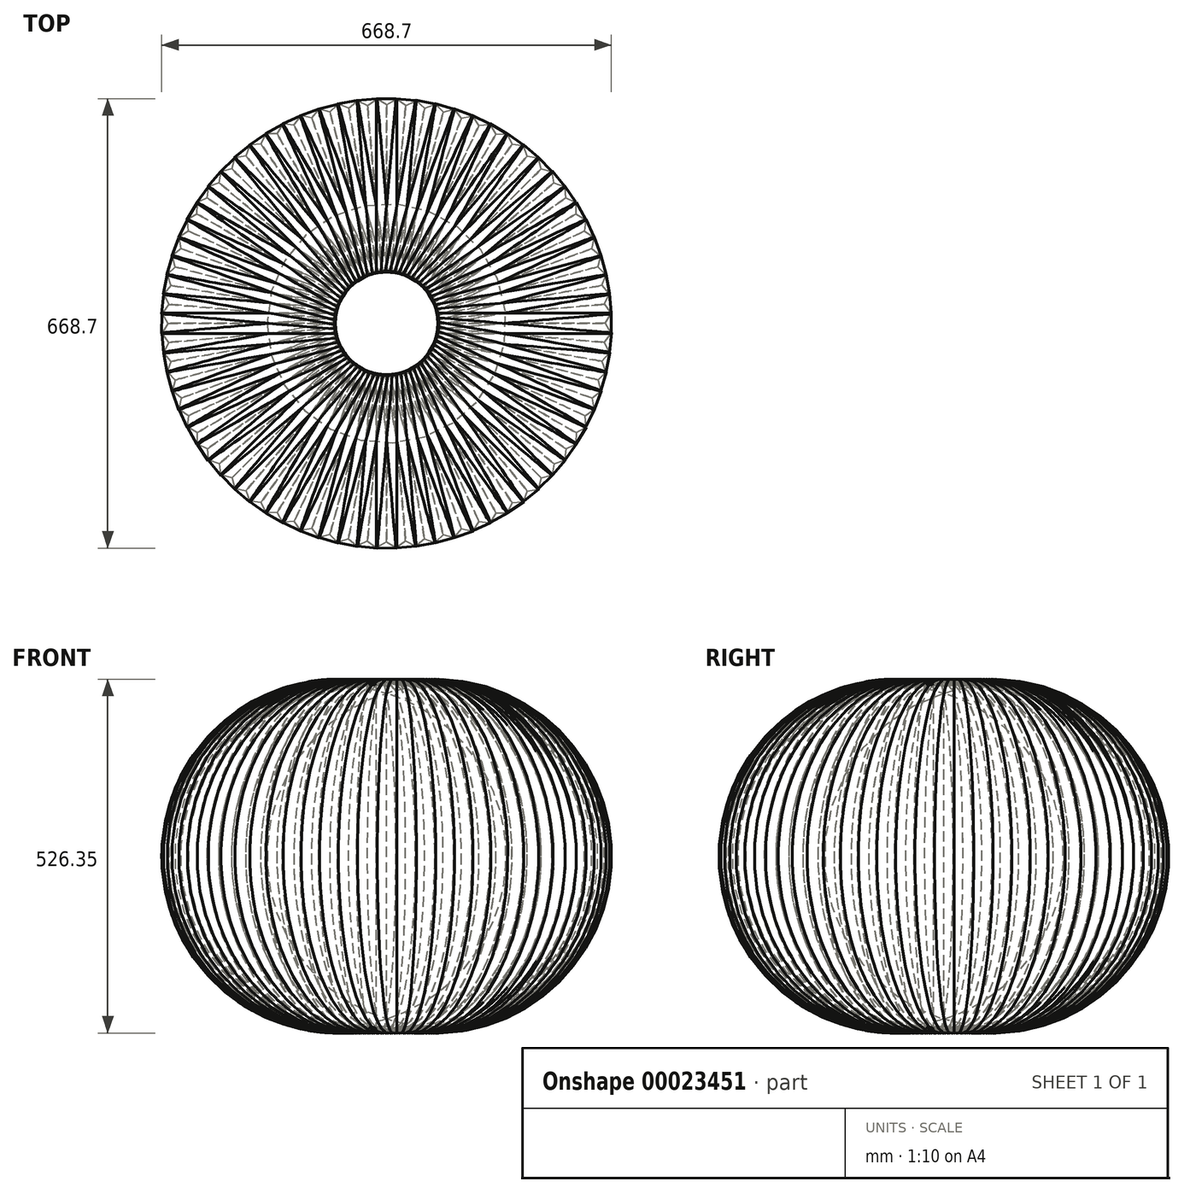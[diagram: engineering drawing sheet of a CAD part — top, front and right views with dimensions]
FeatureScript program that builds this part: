
annotation { "Feature Type Name" : "Feature", "Feature Type Description" : "" }
export const myFeature = defineFeature(function(context is Context, id is Id, definition is map)
    precondition{}
    {
        {
            var Q0;
            Q0=qCreatedBy(makeId("Front.planeOp"),FACE);
            var sketch = newSketch(context, id + "F0", { "sketchPlane" : qUnion([Q0])});
            skLineSegment(sketch, "E0", {"start": v(0, 492.91) * mm, "end": v(0, -560.81) * mm, "construction": true});
            skLineSegment(sketch, "E1.bottom", {"start": v(0, 254) * mm, "end": v(-76.2, 254) * mm});
            skLineSegment(sketch, "E1.top", {"start": v(0, -254) * mm, "end": v(-76.2, -254) * mm});
            skLineSegment(sketch, "E1.left", {"start": v(0, 254) * mm, "end": v(0, -254) * mm});
            skLineSegment(sketch, "E1.right", {"start": v(-76.2, 254) * mm, "end": v(-76.2, -254) * mm});
            skArc(sketch, "E2", {"start": v(-76.2, 254) * mm, "mid": v(-330.2, 0) * mm, "end": v(-76.2, -254) * mm});
            skSolve(sketch);
        }
        {
            var Q0;
            Q0=makeQuery(id+"F0.imprint","IMPRINT",FACE,{"disambiguationData":[TD([[makeQuery(id+"F0.imprint","IMPRINT",EDGE,{"derivedFrom":sQuery(id+"F0.wireOp",EDGE,"E1.right")}),-1.0]])]});
            var Q1;
            Q1=makeQuery(id+"F0.imprint","IMPRINT",FACE,{"disambiguationData":[TD([[makeQuery(id+"F0.imprint","IMPRINT",EDGE,{"derivedFrom":sQuery(id+"F0.wireOp",EDGE,"E1.bottom")}),1.0]])]});
            var Q2;
            Q2=sQuery(id+"F0.wireOp",EDGE,"E0");
            revolve(context, id + "F1", {"entities" : qUnion([Q0, Q1]), "axis" : qUnion([Q2]), "revolveType" : RevolveType.FULL});
        }
        {
            var Q0;
            Q0=qCreatedBy(makeId("Front.planeOp"),FACE);
            var sketch = newSketch(context, id + "F2", { "sketchPlane" : qUnion([Q0])});
            skLineSegment(sketch, "E3", {"start": v(0, 760) * mm, "end": v(0, -293.71) * mm, "construction": true});
            skLineSegment(sketch, "E4.bottom", {"start": v(0, 254) * mm, "end": v(-76.2, 254) * mm});
            skLineSegment(sketch, "E4.top", {"start": v(0, -254) * mm, "end": v(-76.2, -254) * mm});
            skLineSegment(sketch, "E4.left", {"start": v(0, 254) * mm, "end": v(0, -254) * mm});
            skLineSegment(sketch, "E4.right", {"start": v(-76.2, 254) * mm, "end": v(-76.2, -254) * mm});
            skArc(sketch, "E5", {"start": v(-76.2, 254) * mm, "mid": v(-330.2, 0) * mm, "end": v(-76.2, -254) * mm});
            skArc(sketch, "E6", {"start": v(-76.2, 254) * mm, "mid": v(-325.12, 0) * mm, "end": v(-76.2, -254) * mm});
            skLineSegment(sketch, "E7", {"start": v(-71.07, 0) * mm, "end": v(-76.2, -254) * mm, "construction": true});
            skSolve(sketch);
        }
        {
            var Q0;
            Q0=sQuery(id+"F2.wireOp",EDGE,"E4.right");
            cPlane(context, id + "F3", {"entities" : qUnion([Q0]), "cplaneType" : CPlaneType.LINE_ANGLE, "offset" : 152.4 * mm, "angle" : 180 * degree, "width" : 152.4 * mm, "height" : 152.4 * mm});
        }
        {
            var Q0;
            Q0=qCreatedBy(id+"F3.planeOp",FACE);
            var sketch = newSketch(context, id + "F4", { "sketchPlane" : qUnion([Q0])});
            skLineSegment(sketch, "E8", {"start": v(16.43, -254) * mm, "end": v(0, -254) * mm});
            skLineSegment(sketch, "E9", {"start": v(0, -254) * mm, "end": v(0, -244.51) * mm});
            skLineSegment(sketch, "E10", {"start": v(0, -244.51) * mm, "end": v(0, -254) * mm});
            skLineSegment(sketch, "E11", {"start": v(0, -254) * mm, "end": v(0, -261.75) * mm, "construction": true});
            skLineSegment(sketch, "E12", {"start": v(16.43, -254) * mm, "end": v(-17.03, -254.34) * mm});
            skLineSegment(sketch, "E13", {"start": v(15.24, -262.76) * mm, "end": v(0, -254.17) * mm});
            skLineSegment(sketch, "E14", {"start": v(0, -254.17) * mm, "end": v(0, -254) * mm});
            skLineSegment(sketch, "E15", {"start": v(-15.24, -263.18) * mm, "end": v(0, -254.17) * mm});
            skLineSegment(sketch, "E16", {"start": v(-15.24, -263.18) * mm, "end": v(15.24, -262.76) * mm});
            skSolve(sketch);
        }
        {
            var Q0;
            Q0=makeQuery(id+"F4.imprint","IMPRINT",FACE,{"disambiguationData":[TD([[makeQuery(id+"F4.imprint","IMPRINT",EDGE,{"derivedFrom":sQuery(id+"F4.wireOp",EDGE,"E13")}),1.0]])]});
            var Q1;
            Q1=sQuery(id+"F2.wireOp",EDGE,"E6");
            sweep(context, id + "F5", {"profiles" : qUnion([Q0]), "path" : qUnion([Q1])});
        }
        {
            var Q0;
            Q0=makeQuery(id+"F5.opSweep","SWEPT_BODY",BODY,{"disambiguationData":[OSD([sQuery(id+"F2.wireOp",EDGE,"E6"),sQuery(id+"F4.wireOp",EDGE,"E13"),sQuery(id+"F4.wireOp",EDGE,"E15"),sQuery(id+"F4.wireOp",EDGE,"E16")])]});
            var Q1;
            Q1=makeQuery(id+"F5.boolean.opBoolean","COPY",FACE,{"derivedFrom":makeQuery(id+"F5.opSweep","SWEPT_FACE",FACE,{"disambiguationData":[OSD([sQuery(id+"F2.wireOp",EDGE,"E6"),sQuery(id+"F4.wireOp",EDGE,"E15")])]})});
            var Q2;
            Q2=makeQuery(id+"F5.boolean.opBoolean","COPY",FACE,{"derivedFrom":makeQuery(id+"F5.opSweep","SWEPT_FACE",FACE,{"disambiguationData":[OSD([sQuery(id+"F2.wireOp",EDGE,"E6"),sQuery(id+"F4.wireOp",EDGE,"E13")])]})});
            var Q3;
            Q3=sQuery(id+"F0.wireOp",EDGE,"E0");
            circularPattern(context, id + "F6", {"entities" : qUnion([Q0]), "axis" : qUnion([Q3]), "angle" : 360 * degree, "instanceCount" : round(72), "equalSpace" : true});
        }
    });
